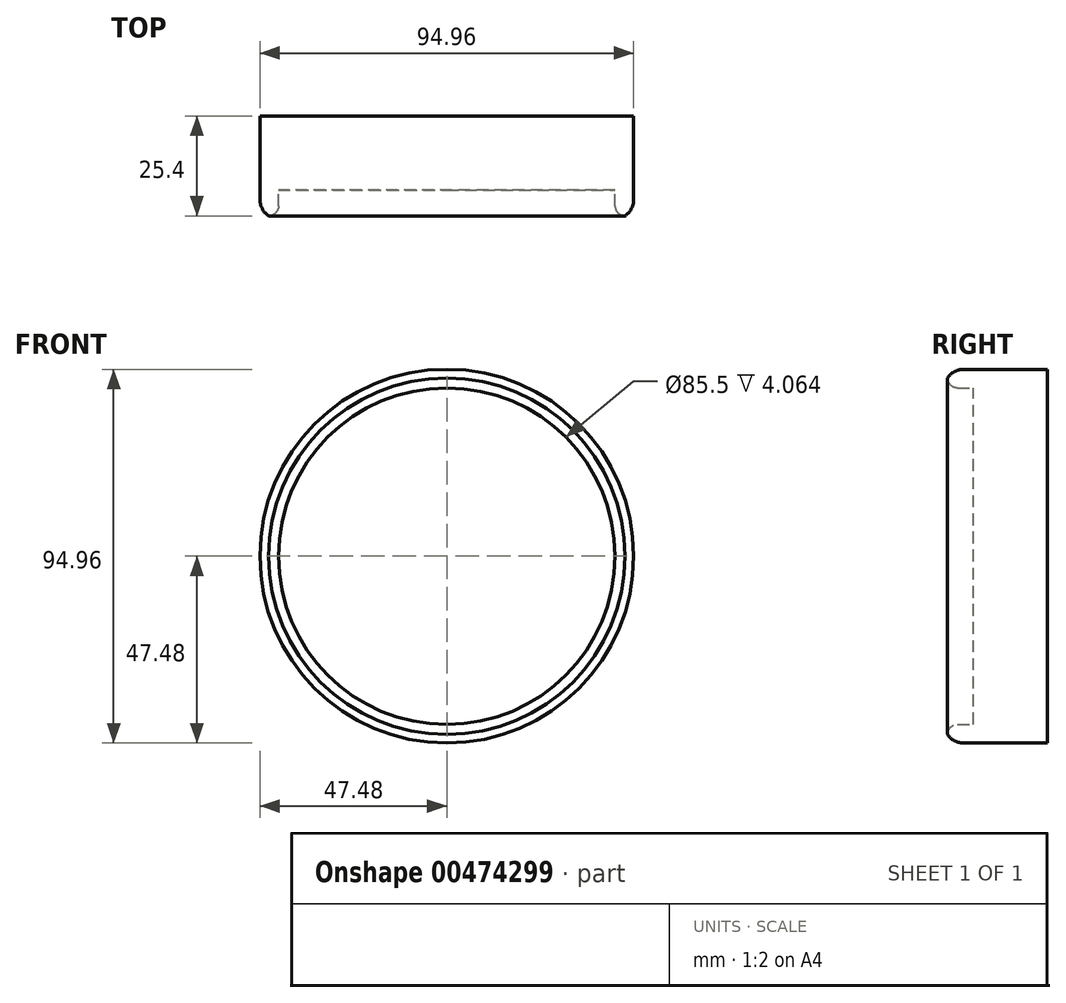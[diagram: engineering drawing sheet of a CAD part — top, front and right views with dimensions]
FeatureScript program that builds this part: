
annotation { "Feature Type Name" : "Feature", "Feature Type Description" : "" }
export const myFeature = defineFeature(function(context is Context, id is Id, definition is map)
    precondition{}
    {
        {
            var Q0;
            Q0=qCreatedBy(makeId("Front.planeOp"),FACE);
            var sketch = newSketch(context, id + "F0", { "sketchPlane" : qUnion([Q0])});
            skCircle(sketch, "E0", {"center": v(0, 0) * mm, "radius": 47.48 * mm});
            skCircle(sketch, "E1", {"center": v(0, 0) * mm, "radius": 42.75 * mm});
            skSolve(sketch);
        }
        {
            var Q0;
            Q0 = qSketchRegion(id + "F0", true);
            extrude(context, id + "F1", {"entities" : qUnion([Q0]), "depth" : 25.4 * mm});
        }
        {
            var Q0;
            Q0=makeQuery(id+"F0.imprint","IMPRINT",FACE,{"disambiguationData":[TD([[makeQuery(id+"F0.imprint","IMPRINT",EDGE,{"derivedFrom":sQuery(id+"F0.wireOp",EDGE,"E1")}),1.0]])]});
            extrude(context, id + "F2", {"entities" : qUnion([Q0]), "operationType" : NewBodyOperationType.ADD, "depth" : 18.8 * mm});
        }
        {
            var Q0;
            Q0=makeQuery(id+"F1.opExtrude","CAP_EDGE",EDGE,{"disambiguationData":[OSD([sQuery(id+"F0.wireOp",EDGE,"E1")])],"isStart":false});
            fillet(context, id + "F3", {"entities" : qUnion([Q0]), "radius" : 2.54 * mm, "tangentPropagation" : true, "allowEdgeOverflow" : false});
        }
        {
            var Q0;
            Q0=makeQuery(id+"F1.opExtrude","CAP_EDGE",EDGE,{"disambiguationData":[OSD([sQuery(id+"F0.wireOp",EDGE,"E0")])],"isStart":false});
            fillet(context, id + "F4", {"entities" : qUnion([Q0]), "radius" : 5.08 * mm, "tangentPropagation" : true, "allowEdgeOverflow" : false});
        }
    });
